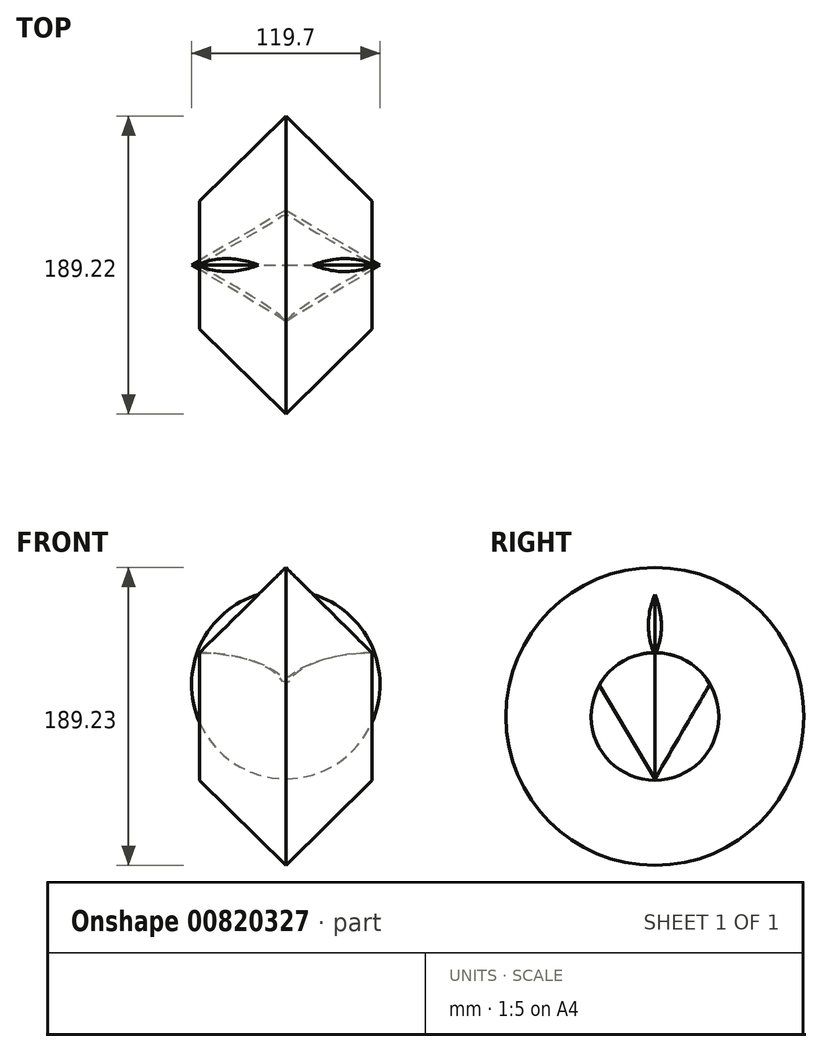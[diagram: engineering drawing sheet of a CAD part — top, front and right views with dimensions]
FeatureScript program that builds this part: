
annotation { "Feature Type Name" : "Feature", "Feature Type Description" : "" }
export const myFeature = defineFeature(function(context is Context, id is Id, definition is map)
    precondition{}
    {
        {
            var Q0;
            Q0=qCreatedBy(makeId("Front.planeOp"),FACE);
            var sketch = newSketch(context, id + "F0", { "sketchPlane" : qUnion([Q0])});
            skLineSegment(sketch, "E0.bottom", {"start": v(-54.81, 20.25) * mm, "end": v(54.81, 20.25) * mm});
            skLineSegment(sketch, "E0.top", {"start": v(-54.81, -20.25) * mm, "end": v(54.81, -20.25) * mm});
            skLineSegment(sketch, "E0.left", {"start": v(-54.81, 20.25) * mm, "end": v(-54.81, -20.25) * mm});
            skLineSegment(sketch, "E0.right", {"start": v(54.81, 20.25) * mm, "end": v(54.81, -20.25) * mm});
            skPoint(sketch, "E0.middle", {"position": v(0, 0) * mm});
            skLineSegment(sketch, "E1", {"start": v(-54.81, 20.25) * mm, "end": v(0, 74.36) * mm});
            skLineSegment(sketch, "E2", {"start": v(0, 74.36) * mm, "end": v(54.81, 20.25) * mm});
            skArc(sketch, "E3", {"start": v(-54.81, -20.25) * mm, "mid": v(0, -68.44) * mm, "end": v(54.81, -20.25) * mm});
            skSolve(sketch);
        }
        {
            var Q0;
            Q0=makeQuery(id+"F0.imprint","IMPRINT",FACE,{"disambiguationData":[TD([[makeQuery(id+"F0.imprint","IMPRINT",EDGE,{"derivedFrom":sQuery(id+"F0.wireOp",EDGE,"E0.bottom")}),1.0]])]});
            var Q1;
            Q1=sQuery(id+"F0.wireOp",EDGE,"E0.top");
            revolve(context, id + "F1", {"surfaceOperationType" : NewSurfaceOperationType.NEW, "entities" : qUnion([Q0]), "axis" : qUnion([Q1]), "revolveType" : RevolveType.FULL});
        }
        {
            var Q0;
            Q0=qCreatedBy(makeId("Right.planeOp"),FACE);
            var sketch = newSketch(context, id + "F2", { "sketchPlane" : qUnion([Q0])});
            skLineSegment(sketch, "E4", {"start": v(34.82, 0) * mm, "end": v(0, -59.85) * mm});
            skLineSegment(sketch, "E5", {"start": v(0, -59.85) * mm, "end": v(-35.51, 0) * mm});
            skLineSegment(sketch, "E6", {"start": v(-35.51, 0) * mm, "end": v(34.82, 0) * mm});
            skSolve(sketch);
        }
        {
            var Q0;
            Q0=makeQuery(id+"F2.imprint","IMPRINT",FACE,{"disambiguationData":[TD([[makeQuery(id+"F2.imprint","IMPRINT",EDGE,{"derivedFrom":sQuery(id+"F2.wireOp",EDGE,"E4")}),-1.0]])]});
            var Q1;
            Q1=sQuery(id+"F2.wireOp",EDGE,"E6");
            revolve(context, id + "F3", {"operationType" : NewBodyOperationType.ADD, "surfaceOperationType" : NewSurfaceOperationType.NEW, "entities" : qUnion([Q0]), "axis" : qUnion([Q1]), "revolveType" : RevolveType.FULL});
        }
    });
